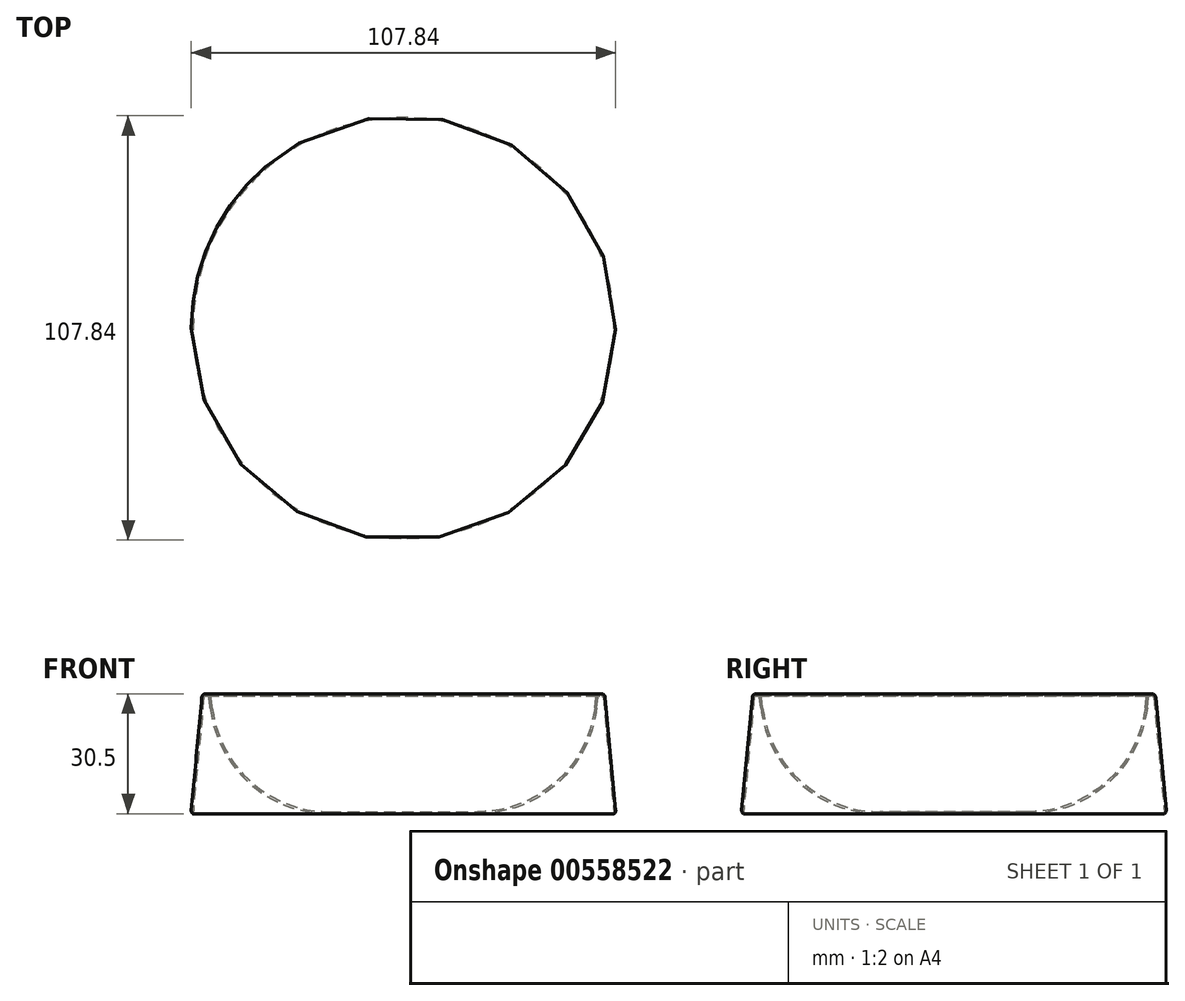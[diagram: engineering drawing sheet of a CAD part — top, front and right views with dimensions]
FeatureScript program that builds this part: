
annotation { "Feature Type Name" : "Feature", "Feature Type Description" : "" }
export const myFeature = defineFeature(function(context is Context, id is Id, definition is map)
    precondition{}
    {
        {
            var Q0;
            Q0=qCreatedBy(makeId("Front.planeOp"),FACE);
            var sketch = newSketch(context, id + "F0", { "sketchPlane" : qUnion([Q0])});
            skLineSegment(sketch, "E0", {"start": v(54, -0.5) * mm, "end": v(51.25, 29.09) * mm});
            skLineSegment(sketch, "E1", {"start": v(50.25, 30) * mm, "end": v(49.9, 30) * mm});
            skLineSegment(sketch, "E2", {"start": v(48.91, 29.12) * mm, "end": v(48.6, 26.44) * mm});
            skLineSegment(sketch, "E3", {"start": v(18.8, 0) * mm, "end": v(0, 0) * mm});
            skArc(sketch, "E4.filletArc", {"start": v(18.8, 0) * mm, "mid": v(38.72, 7.56) * mm, "end": v(48.6, 26.44) * mm});
            skLineSegment(sketch, "E5.0", {"start": v(53.5, -0.5) * mm, "end": v(50.75, 29.05) * mm});
            skLineSegment(sketch, "E5.1", {"start": v(49.4, 29.06) * mm, "end": v(49.09, 26.38) * mm});
            skArc(sketch, "E5.2", {"start": v(18.8, -0.5) * mm, "mid": v(39.05, 7.19) * mm, "end": v(49.09, 26.38) * mm});
            skLineSegment(sketch, "E5.3", {"start": v(18.8, -0.5) * mm, "end": v(0, -0.5) * mm});
            skLineSegment(sketch, "E6", {"start": v(0, 0) * mm, "end": v(0, -0.5) * mm});
            skLineSegment(sketch, "E7.0", {"start": v(50.25, 29.5) * mm, "end": v(49.9, 29.5) * mm});
            skLineSegment(sketch, "E8", {"start": v(53.5, -0.5) * mm, "end": v(54, -0.5) * mm});
            skLineSegment(sketch, "E9", {"start": v(0, 0) * mm, "end": v(0, 56.28) * mm, "construction": true});
            skArc(sketch, "E10.filletArc", {"start": v(49.9, 29.5) * mm, "mid": v(49.57, 29.37) * mm, "end": v(49.4, 29.06) * mm});
            skArc(sketch, "E11.filletArc", {"start": v(50.75, 29.05) * mm, "mid": v(50.59, 29.37) * mm, "end": v(50.25, 29.5) * mm});
            skArc(sketch, "E12.filletArc", {"start": v(49.9, 30) * mm, "mid": v(49.24, 29.75) * mm, "end": v(48.91, 29.12) * mm});
            skArc(sketch, "E13.filletArc", {"start": v(51.25, 29.09) * mm, "mid": v(50.92, 29.74) * mm, "end": v(50.25, 30) * mm});
            skSolve(sketch);
        }
        {
            var Q0;
            Q0=makeQuery(id+"F0.imprint","IMPRINT",FACE,{"disambiguationData":[TD([[makeQuery(id+"F0.imprint","IMPRINT",EDGE,{"derivedFrom":sQuery(id+"F0.wireOp",EDGE,"E0")}),1.0]])]});
            var Q1;
            Q1=sQuery(id+"F0.wireOp",EDGE,"E9");
            revolve(context, id + "F1", {"entities" : qUnion([Q0]), "axis" : qUnion([Q1]), "revolveType" : RevolveType.FULL});
        }
        {
            var Q0;
            Q0=makeQuery(id+"F1.opRevolve","SWEPT_EDGE",EDGE,{"disambiguationData":[OSD([sQuery(id+"F0.wireOp",EDGE,"E0"),sQuery(id+"F0.wireOp",EDGE,"E1")])]});
            var Q1;
            Q1=makeQuery(id+"F1.opRevolve","SWEPT_EDGE",EDGE,{"disambiguationData":[OSD([sQuery(id+"F0.wireOp",EDGE,"E1"),sQuery(id+"F0.wireOp",EDGE,"E2")])]});
            fillet(context, id + "F2", {"entities" : qUnion([Q0, Q1]), "radius" : 1 * mm, "tangentPropagation" : true, "allowEdgeOverflow" : false});
        }
    });
